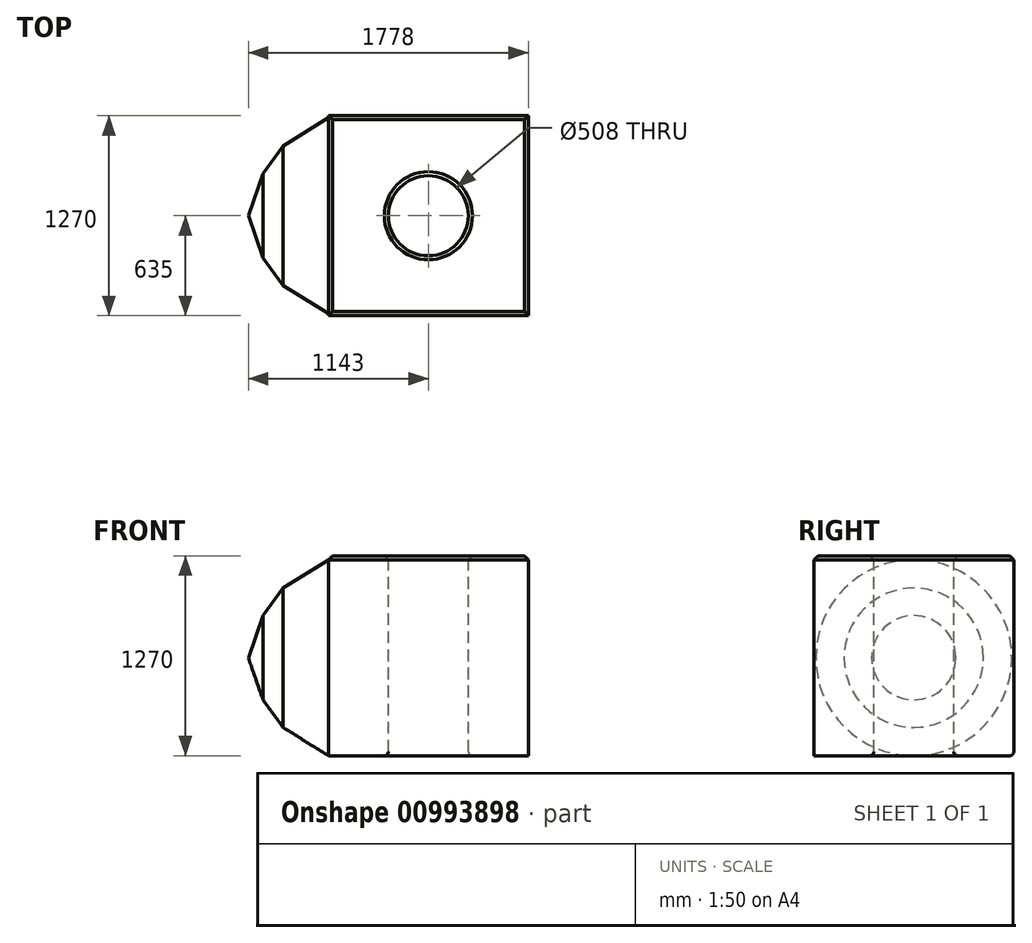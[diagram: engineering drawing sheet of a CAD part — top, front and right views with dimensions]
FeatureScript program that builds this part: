
annotation { "Feature Type Name" : "Feature", "Feature Type Description" : "" }
export const myFeature = defineFeature(function(context is Context, id is Id, definition is map)
    precondition{}
    {
        {
            var Q0;
            Q0=qCreatedBy(makeId("Top.planeOp"),FACE);
            var sketch = newSketch(context, id + "F0", { "sketchPlane" : qUnion([Q0])});
            skLineSegment(sketch, "E0.bottom", {"start": v(635, -635) * mm, "end": v(-635, -635) * mm});
            skLineSegment(sketch, "E0.top", {"start": v(635, 635) * mm, "end": v(-635, 635) * mm});
            skLineSegment(sketch, "E0.left", {"start": v(635, -635) * mm, "end": v(635, 635) * mm});
            skLineSegment(sketch, "E0.right", {"start": v(-635, -635) * mm, "end": v(-635, 635) * mm});
            skPoint(sketch, "E0.middle", {"position": v(0, 0) * mm});
            skSolve(sketch);
        }
        {
            var Q0;
            Q0=makeQuery(id+"F0.imprint","IMPRINT",FACE,{"disambiguationData":[TD([[makeQuery(id+"F0.imprint","IMPRINT",EDGE,{"derivedFrom":sQuery(id+"F0.wireOp",EDGE,"E0.bottom")}),-1.0]])]});
            extrude(context, id + "F1", {"entities" : qUnion([Q0]), "depth" : 1270 * mm, "offsetDistance" : 25.4 * mm});
        }
        {
            var Q0;
            Q0=makeQuery(id+"F1.opExtrude","CAP_FACE",FACE,{"disambiguationData":[OSD([sQuery(id+"F0.wireOp",EDGE,"E0.bottom"),sQuery(id+"F0.wireOp",EDGE,"E0.top"),sQuery(id+"F0.wireOp",EDGE,"E0.left"),sQuery(id+"F0.wireOp",EDGE,"E0.right")])],"isStart":false});
            var sketch = newSketch(context, id + "F2", { "sketchPlane" : qUnion([Q0])});
            skCircle(sketch, "E1", {"center": v(0, 0) * mm, "radius": 254 * mm});
            skSolve(sketch);
        }
        {
            var Q0;
            Q0=makeQuery(id+"F2.imprint","IMPRINT",FACE,{"disambiguationData":[TD([[makeQuery(id+"F2.imprint","IMPRINT",EDGE,{"derivedFrom":sQuery(id+"F2.wireOp",EDGE,"E1")}),1.0]])]});
            extrude(context, id + "F3", {"entities" : qUnion([Q0]), "operationType" : NewBodyOperationType.REMOVE, "endBound" : BoundingType.THROUGH_ALL, "oppositeDirection" : true, "depth" : 25.4 * mm, "offsetDistance" : 25.4 * mm});
        }
        {
            var Q0;
            Q0=makeQuery(id+"F1.opExtrude","CAP_FACE",FACE,{"disambiguationData":[OSD([sQuery(id+"F0.wireOp",EDGE,"E0.bottom"),sQuery(id+"F0.wireOp",EDGE,"E0.top"),sQuery(id+"F0.wireOp",EDGE,"E0.left"),sQuery(id+"F0.wireOp",EDGE,"E0.right")])],"isStart":false});
            chamfer(context, id + "F4", {"entities" : qUnion([Q0]), "width" : 25.4 * mm, "tangentPropagation" : true});
        }
        {
            var Q0;
            Q0=makeQuery(id+"F3.boolean.opBoolean","INTERSECT",EDGE,{"derivedFrom":[makeQuery(id+"F1.opExtrude","CAP_FACE",FACE,{"disambiguationData":[OSD([sQuery(id+"F0.wireOp",EDGE,"E0.bottom"),sQuery(id+"F0.wireOp",EDGE,"E0.top"),sQuery(id+"F0.wireOp",EDGE,"E0.left"),sQuery(id+"F0.wireOp",EDGE,"E0.right")])],"isStart":true}),makeQuery(id+"F3.opExtrude","SWEPT_FACE",FACE,{"disambiguationData":[OSD([sQuery(id+"F2.wireOp",EDGE,"E1")])]})]});
            fillet(context, id + "F5", {"entities" : qUnion([Q0]), "radius" : 25.4 * mm, "tangentPropagation" : true, "allowEdgeOverflow" : false});
        }
        {
            var Q0;
            Q0=makeQuery(id+"F1.opExtrude","CAP_EDGE",EDGE,{"disambiguationData":[OSD([sQuery(id+"F0.wireOp",EDGE,"E0.top")])],"isStart":true});
            fillet(context, id + "F6", {"entities" : qUnion([Q0]), "radius" : 25.4 * mm, "tangentPropagation" : true, "allowEdgeOverflow" : false});
        }
        {
            var Q0;
            Q0=qCreatedBy(makeId("Front.planeOp"),FACE);
            var sketch = newSketch(context, id + "F7", { "sketchPlane" : qUnion([Q0])});
            skLineSegment(sketch, "E2.0", {"start": v(-635, 1244.6) * mm, "end": v(-635, 0) * mm});
            skLineSegment(sketch, "E3", {"start": v(-635, 622.3) * mm, "end": v(-1143, 622.3) * mm});
            skLineSegment(sketch, "E4", {"start": v(-1143, 622.3) * mm, "end": v(-1050.37, 354.8) * mm});
            skLineSegment(sketch, "E5", {"start": v(-1050.37, 354.8) * mm, "end": v(-922.3, 179.88) * mm});
            skLineSegment(sketch, "E6", {"start": v(-922.3, 179.88) * mm, "end": v(-635, 0) * mm});
            skSolve(sketch);
        }
        {
            var Q0;
            {var subQ0=sQuery(id+"F7.wireOp",EDGE,"E3");Q0=makeQuery(id+"F7.imprint","IMPRINT",FACE,{"disambiguationData":[TD([[makeQuery(id+"F7.imprint","IMPRINT",EDGE,{"derivedFrom":subQ0}),1.0]])]});}
            var Q1;
            Q1=sQuery(id+"F7.wireOp",EDGE,"E3");
            revolve(context, id + "F8", {"operationType" : NewBodyOperationType.ADD, "surfaceOperationType" : NewSurfaceOperationType.NEW, "entities" : qUnion([Q0]), "axis" : qUnion([Q1]), "revolveType" : RevolveType.FULL});
        }
    });
